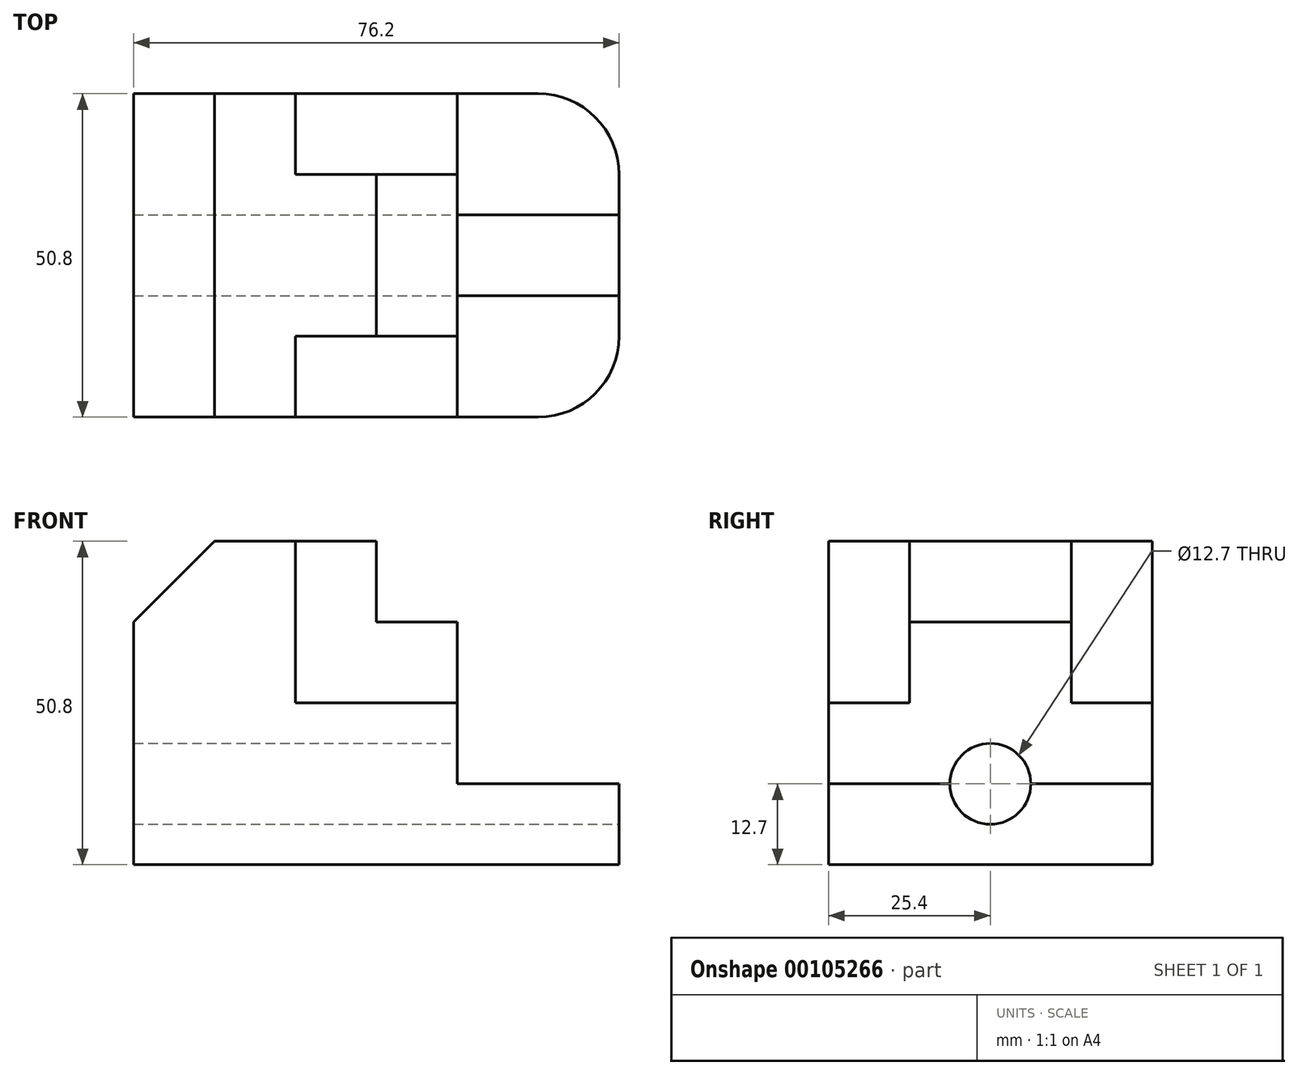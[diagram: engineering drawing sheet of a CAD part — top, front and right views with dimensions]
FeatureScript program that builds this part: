
annotation { "Feature Type Name" : "Feature", "Feature Type Description" : "" }
export const myFeature = defineFeature(function(context is Context, id is Id, definition is map)
    precondition{}
    {
        {
            var Q0;
            Q0=qCreatedBy(makeId("Front.planeOp"),FACE);
            var sketch = newSketch(context, id + "F0", { "sketchPlane" : qUnion([Q0])});
            skLineSegment(sketch, "E0", {"start": v(0, 0) * mm, "end": v(0, 38.1) * mm});
            skLineSegment(sketch, "E1", {"start": v(0, 38.1) * mm, "end": v(12.7, 50.8) * mm});
            skLineSegment(sketch, "E2", {"start": v(12.7, 50.8) * mm, "end": v(25.4, 50.8) * mm});
            skLineSegment(sketch, "E3", {"start": v(25.4, 50.8) * mm, "end": v(25.4, 25.4) * mm});
            skLineSegment(sketch, "E4", {"start": v(25.4, 25.4) * mm, "end": v(50.8, 25.4) * mm});
            skLineSegment(sketch, "E5", {"start": v(50.8, 25.4) * mm, "end": v(50.8, 12.7) * mm});
            skLineSegment(sketch, "E6", {"start": v(50.8, 12.7) * mm, "end": v(76.2, 12.7) * mm});
            skLineSegment(sketch, "E7", {"start": v(76.2, 12.7) * mm, "end": v(76.2, 0) * mm});
            skLineSegment(sketch, "E8", {"start": v(76.2, 0) * mm, "end": v(0, 0) * mm});
            skLineSegment(sketch, "E9", {"start": v(25.4, 50.8) * mm, "end": v(38.1, 50.8) * mm});
            skLineSegment(sketch, "E10", {"start": v(38.1, 50.8) * mm, "end": v(38.1, 38.1) * mm});
            skLineSegment(sketch, "E11", {"start": v(38.1, 38.1) * mm, "end": v(50.8, 38.1) * mm});
            skLineSegment(sketch, "E12", {"start": v(50.8, 38.1) * mm, "end": v(50.8, 25.4) * mm});
            skSolve(sketch);
        }
        {
            var Q0;
            Q0=makeQuery(id+"F0.imprint","IMPRINT",FACE,{"disambiguationData":[TD([[makeQuery(id+"F0.imprint","IMPRINT",EDGE,{"derivedFrom":sQuery(id+"F0.wireOp",EDGE,"E0")}),-1.0]])]});
            extrude(context, id + "F1", {"entities" : qUnion([Q0]), "endBound" : BoundingType.SYMMETRIC, "depth" : 50.8 * mm});
        }
        {
            var Q0;
            Q0=makeQuery(id+"F0.imprint","IMPRINT",FACE,{"disambiguationData":[TD([[makeQuery(id+"F0.imprint","IMPRINT",EDGE,{"derivedFrom":sQuery(id+"F0.wireOp",EDGE,"E3")}),1.0]])]});
            extrude(context, id + "F2", {"entities" : qUnion([Q0]), "operationType" : NewBodyOperationType.ADD, "endBound" : BoundingType.SYMMETRIC, "depth" : 25.4 * mm});
        }
        {
            var Q0;
            Q0=makeQuery(id+"F1.opExtrude","CAP_EDGE",EDGE,{"disambiguationData":[OSD([sQuery(id+"F0.wireOp",EDGE,"E7")])],"isStart":false});
            var Q1;
            Q1=makeQuery(id+"F1.opExtrude","CAP_EDGE",EDGE,{"disambiguationData":[OSD([sQuery(id+"F0.wireOp",EDGE,"E7")])],"isStart":true});
            fillet(context, id + "F3", {"entities" : qUnion([Q0, Q1]), "radius" : 12.7 * mm, "tangentPropagation" : true, "allowEdgeOverflow" : false});
        }
        {
            var Q0;
            Q0=makeQuery(id+"F1.opExtrude","SWEPT_FACE",FACE,{"disambiguationData":[OSD([sQuery(id+"F0.wireOp",EDGE,"E7")])]});
            var sketch = newSketch(context, id + "F4", { "sketchPlane" : qUnion([Q0])});
            skCircle(sketch, "E13", {"center": v(0, 12.7) * mm, "radius": 6.35 * mm});
            skSolve(sketch);
        }
        {
            var Q0;
            {var subQ0=sQuery(id+"F4.wireOp",EDGE,"E13");var subQ1=makeQuery(id+"F1.opExtrude","SWEPT_EDGE",EDGE,{"disambiguationData":[OSD([sQuery(id+"F0.wireOp",EDGE,"E6"),sQuery(id+"F0.wireOp",EDGE,"E7")])]});var subQ2=makeQuery(id+"F4.imprint","INTERSECT",VERTEX,{"disambiguationData":[OD(0.0)],"derivedFrom":[subQ1,subQ0]});Q0=makeQuery(id+"F4.imprint","IMPRINT",FACE,{"disambiguationData":[TD([[makeQuery(id+"F4.imprint","IMPRINT",EDGE,{"disambiguationData":[TD([[subQ2,-1.0]])],"derivedFrom":subQ0}),1.0]])]});}
            var Q1;
            {var subQ0=sQuery(id+"F4.wireOp",EDGE,"E13");var subQ1=makeQuery(id+"F1.opExtrude","SWEPT_EDGE",EDGE,{"disambiguationData":[OSD([sQuery(id+"F0.wireOp",EDGE,"E6"),sQuery(id+"F0.wireOp",EDGE,"E7")])]});var subQ2=makeQuery(id+"F4.imprint","INTERSECT",VERTEX,{"disambiguationData":[OD(0.0)],"derivedFrom":[subQ1,subQ0]});Q1=makeQuery(id+"F4.imprint","IMPRINT",FACE,{"disambiguationData":[TD([[makeQuery(id+"F4.imprint","IMPRINT",EDGE,{"disambiguationData":[TD([[subQ2,1.0]])],"derivedFrom":subQ0}),1.0]])]});}
            extrude(context, id + "F5", {"entities" : qUnion([Q0, Q1]), "operationType" : NewBodyOperationType.REMOVE, "endBound" : BoundingType.THROUGH_ALL, "oppositeDirection" : true, "depth" : 25.4 * mm});
        }
    });
